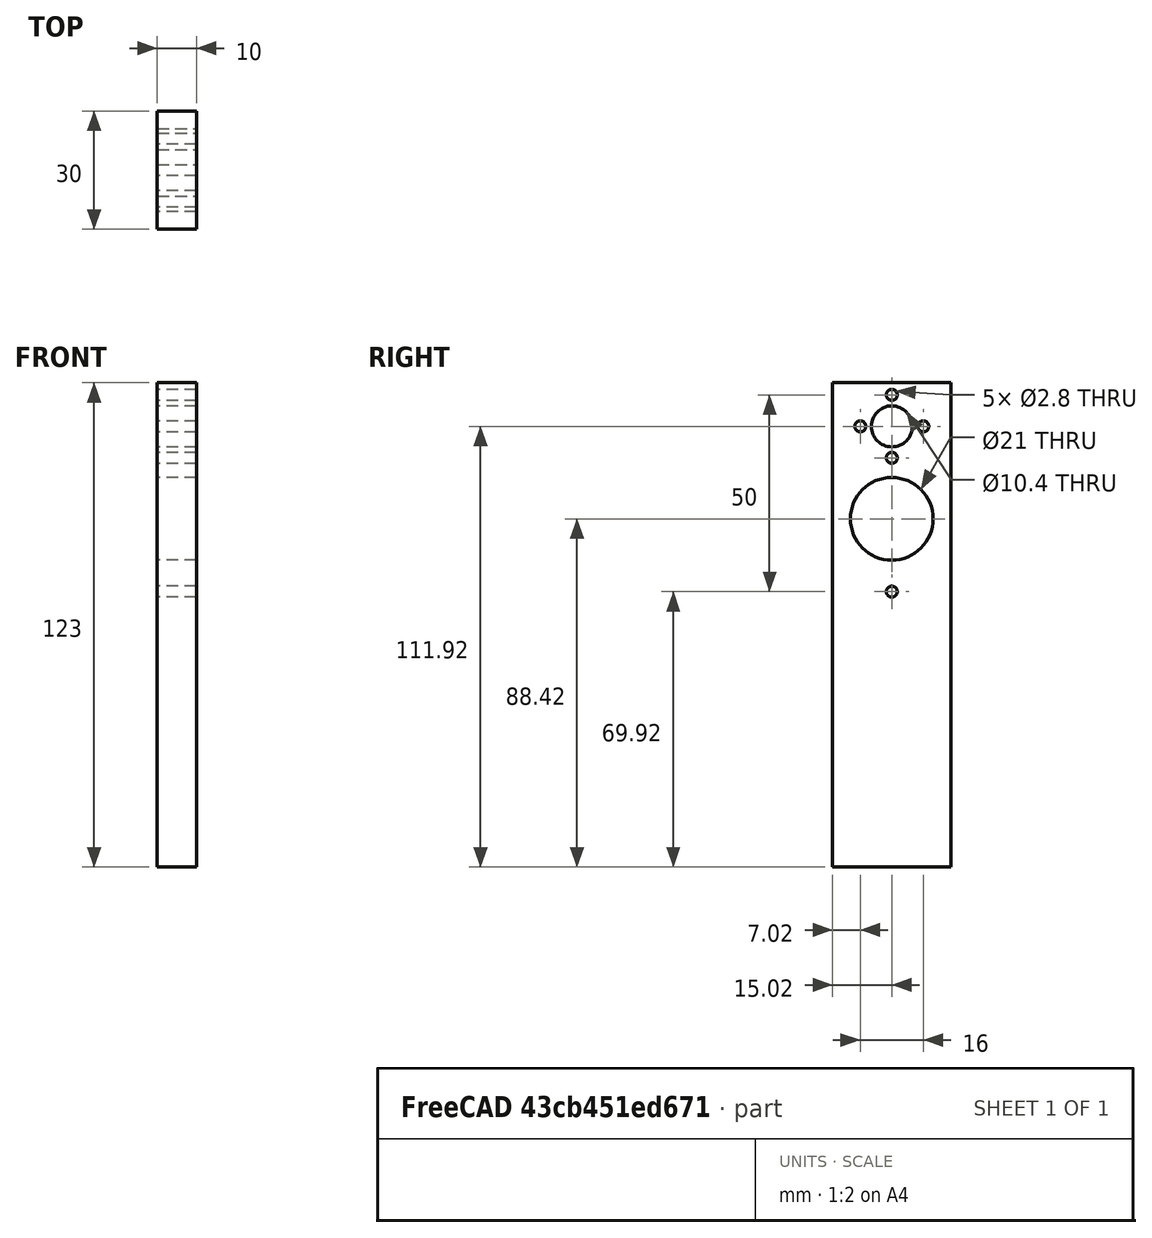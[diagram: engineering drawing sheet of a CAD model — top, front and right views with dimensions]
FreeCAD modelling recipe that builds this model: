
FCSTD DOCUMENT  (FreeCAD 0.18.4R)
Label: cnc
License: All rights reserved
LicenseURL: http://en.wikipedia.org/wiki/All_rights_reserved
objects: Sketcher::SketchObject×4, Mesh::Feature×1, Part::Feature×1, PartDesign::CoordinateSystem×1, PartDesign::Pad×1, PartDesign::Body×1
note: 9 computed .brp shape members not serialized (recipe doc carries the construction recipe); baked Part::Feature solids carry a one-line shape summary decoded from their .brp

FEATURE [Mesh::Feature] x_axis_carriage_left
  Placement = pos=(217,0,0.5) rot=(0,0,1;0rad)
FEATURE [Part::Feature] MR_Points
  shape: bbox 50 x 30 x 123 mm, 0 faces, 0 solids (baked)
FEATURE [Sketcher::SketchObject] Sketch  label="outer sketch"
  Placement = pos=(0,0,0) rot=(-1,0,0;1.5708rad)
  sketch-geometry (3):
    g0: Circle CenterX=-242 CenterY=149.125 CenterZ=0 NormalX=0 NormalY=1e-16 NormalZ=1 AngleXU=-1.5708 Radius=7
    g1: Circle CenterX=-242 CenterY=88.4999 CenterZ=0 NormalX=0 NormalY=1e-16 NormalZ=1 AngleXU=-1.5708 Radius=7
    g2: Circle CenterX=-242 CenterY=118.5 CenterZ=0 NormalX=0 NormalY=-1e-16 NormalZ=-1 AngleXU=-1.5708 Radius=13
  constraints (3):
    c: Radius(g0) = 7
    c: Equal(g0,g1)
    c: Radius(g2) = 13
FEATURE [Sketcher::SketchObject] Sketch001  label="inner sketch"
  Placement = pos=(0,0,0) rot=(-1,0,0;1.5708rad)
  sketch-geometry (3):
    g0: Circle CenterX=-242 CenterY=118.5 CenterZ=0 NormalX=0 NormalY=1e-16 NormalZ=1 AngleXU=-1.5708 Radius=11
    g1: Circle CenterX=-242 CenterY=88.5 CenterZ=0 NormalX=0 NormalY=1e-16 NormalZ=1 AngleXU=-1.5708 Radius=6
    g2: Circle CenterX=-242 CenterY=149.125 CenterZ=0 NormalX=0 NormalY=1e-16 NormalZ=1 AngleXU=-1.5708 Radius=6
  constraints (3):
    c: Radius(g0) = 11
    c: Radius(g1) = 6
    c: Equal(g1,g2)
FEATURE [Sketcher::SketchObject] Sketch003  label="inner side sketch"
  Placement = pos=(-1,0,0) rot=(0,1,0;1.5708rad)
  sketch-geometry (11):
    g0: Circle CenterX=38.08 CenterY=15.02 CenterZ=0 NormalX=1e-16 NormalY=0 NormalZ=1 AngleXU=1.5708 Radius=1.4
    g1: Circle CenterX=69.58 CenterY=15.02 CenterZ=0 NormalX=1e-16 NormalY=0 NormalZ=1 AngleXU=1.5708 Radius=10.5
    g2: Circle CenterX=46.08 CenterY=15.02 CenterZ=0 NormalX=1e-16 NormalY=0 NormalZ=1 AngleXU=1.5708 Radius=5.2
    g3: Circle CenterX=88.08 CenterY=15.02 CenterZ=0 NormalX=1e-16 NormalY=0 NormalZ=1 AngleXU=1.5708 Radius=1.4
    g4: Circle CenterX=46.08 CenterY=7.02 CenterZ=0 NormalX=1e-16 NormalY=0 NormalZ=1 AngleXU=1.5708 Radius=1.4
    g5: Circle CenterX=54.08 CenterY=15.02 CenterZ=0 NormalX=1e-16 NormalY=0 NormalZ=1 AngleXU=1.5708 Radius=1.4
    g6: Circle CenterX=46.08 CenterY=23.02 CenterZ=0 NormalX=1e-16 NormalY=0 NormalZ=1 AngleXU=1.5708 Radius=1.4
    g7: LineSegment StartX=35 StartY=30 StartZ=0 EndX=158 EndY=30 EndZ=0
    g8: LineSegment StartX=158 StartY=30 StartZ=0 EndX=158 EndY=0 EndZ=0
    g9: LineSegment StartX=158 StartY=0 StartZ=0 EndX=35 EndY=0 EndZ=0
    g10: LineSegment StartX=35 StartY=0 StartZ=0 EndX=35 EndY=30 EndZ=0
  constraints (30):
    c: Radius(g0) = 1.4
    c: Radius(g1) = 10.5
    c: Radius(g2) = 5.2
    c: Equal(g0, g3-g6) x4
    c: DistanceX(g2,g1) = 23.5
    c: DistanceX(g-1,g2) = 46.08
    c: DistanceY(g0,g2) = 0
    c: DistanceY(g5,g2) = 0
    c: DistanceX(g0,g2) = 8
    c: DistanceX(g2,g5) = 8
    c: DistanceY(g4,g2) = 8
    c: DistanceY(g2,g6) = 8
    c: DistanceX(g2,g6) = 0
    c: DistanceX(g2,g4) = 0
    c: DistanceY(g2,g1) = 0
    c: DistanceY(g1,g3) = 0
    c: DistanceX(g1,g3) = 18.5
    c: DistanceY(g-1,g2) = 15.02
    c: Coincident(g7,g8)
    c: Coincident(g8,g9)
    c: Coincident(g9,g10)
    c: Coincident(g10,g7)
    c: Horizontal(g7)
    c: Horizontal(g9)
    c: Vertical(g8)
    c: Vertical(g10)
    c: DistanceX(g7,g7) = 123
    c: DistanceY(g8,g8) = 30
    c: DistanceY(g9,g-1) = 0
    c: DistanceX(g-1,g9) = 35
FEATURE [Sketcher::SketchObject] Sketch005  label="outside side sketch"
  Placement = pos=(0,0,0) rot=(0,1,0;1.5708rad)
  sketch-geometry (11):
    g0: Circle CenterX=38.08 CenterY=15.2 CenterZ=0 NormalX=1e-16 NormalY=0 NormalZ=1 AngleXU=1.5708 Radius=2.4
    g1: Circle CenterX=46.08 CenterY=7.2 CenterZ=0 NormalX=1e-16 NormalY=0 NormalZ=1 AngleXU=1.5708 Radius=2.4
    g2: Circle CenterX=46.08 CenterY=23.2 CenterZ=0 NormalX=-1e-16 NormalY=0 NormalZ=-1 AngleXU=0 Radius=2.4
    g3: Circle CenterX=54.08 CenterY=15.2 CenterZ=0 NormalX=-1e-16 NormalY=0 NormalZ=-1 AngleXU=0 Radius=2.4
    g4: Circle CenterX=46.08 CenterY=15.2 CenterZ=0 NormalX=1e-16 NormalY=0 NormalZ=1 AngleXU=1.5708 Radius=6.2
    g5: Circle CenterX=88.08 CenterY=15.2 CenterZ=0 NormalX=-1e-16 NormalY=0 NormalZ=-1 AngleXU=0 Radius=2.4
    g6: Circle CenterX=69.58 CenterY=15.2 CenterZ=0 NormalX=-1e-16 NormalY=0 NormalZ=-1 AngleXU=0 Radius=11.5
    g7: LineSegment StartX=35 StartY=30 StartZ=0 EndX=158 EndY=30 EndZ=0
    g8: LineSegment StartX=158 StartY=30 StartZ=0 EndX=158 EndY=0 EndZ=0
    g9: LineSegment StartX=158 StartY=0 StartZ=0 EndX=35 EndY=0 EndZ=0
    g10: LineSegment StartX=35 StartY=0 StartZ=0 EndX=35 EndY=30 EndZ=0
  constraints (33):
    c: Radius(g0) = 2.4
    c: Equal(g0,g1)
    c: Equal(g0,g2)
    c: Equal(g0,g3)
    c: Radius(g4) = 6.2
    c: Equal(g0,g5)
    c: Radius(g6) = 11.5
    c: DistanceY(g4,g2) = 8
    c: DistanceY(g1,g4) = 8
    c: DistanceX(g0,g4) = 8
    c: DistanceX(g4,g3) = 8
    c: DistanceX(g1,g2) = 0
    c: DistanceY(g3,g0) = 0
    c: DistanceX(g6,g5) = 18.5
    c: DistanceX(g4,g6) = 23.5
    c: DistanceY(g6,g5) = 0
    c: DistanceY(g6,g4) = 0
    c: DistanceX(g1,g4) = 0
    c: DistanceY(g4,g0) = 0
    c: DistanceX(g-1,g4) = 46.08
    c: DistanceY(g-1,g4) = 15.2
    c: Coincident(g7,g8)
    c: Coincident(g8,g9)
    c: Coincident(g9,g10)
    c: Coincident(g10,g7)
    c: Horizontal(g7)
    c: Horizontal(g9)
    c: Vertical(g8)
    c: Vertical(g10)
    c: DistanceX(g7,g7) = 123
    c: DistanceY(g8,g8) = 30
    c: DistanceX(g-1,g9) = 35
    c: DistanceY(g-1,g9) = 0
FEATURE [PartDesign::CoordinateSystem] Local_CS
  AttacherType = Attacher::AttachEngine3D
  AttachmentOffset = pos=(0,0,35) rot=(0,0,1;0rad)
  MapMode = 4
  Placement = pos=(7.8e-15,0,-35) rot=(0.707107,0.707107,0;3.14159rad)
  Support = -> [Sketch005]
FEATURE [PartDesign::Pad] Pad
  Length = 10
  Length2 = 100
  Placement = pos=(-1,0,0) rot=(0,1,0;1.5708rad)
  Profile = -> Sketch003
  Type = 0
FEATURE [PartDesign::Body] Body
  Group = -> [Sketch005,Local_CS,Sketch003,Pad]
  Origin = -> Origin
  Tip = -> Pad
